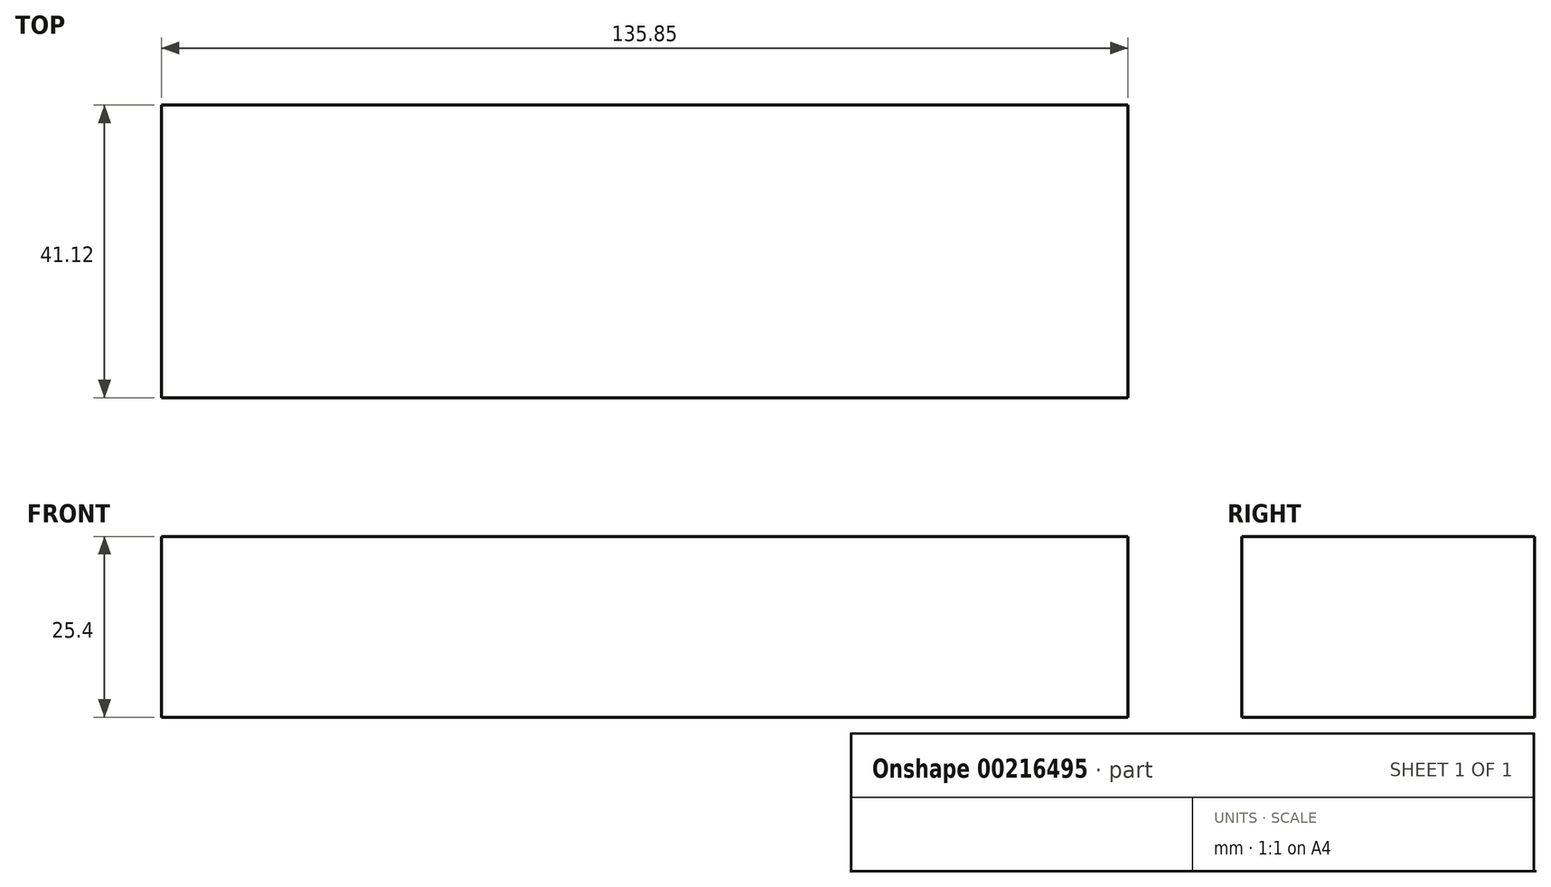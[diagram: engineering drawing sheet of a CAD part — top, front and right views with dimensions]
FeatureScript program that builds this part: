
annotation { "Feature Type Name" : "Feature", "Feature Type Description" : "" }
export const myFeature = defineFeature(function(context is Context, id is Id, definition is map)
    precondition{}
    {
        {
            var Q0;
            Q0=qCreatedBy(makeId("Top.planeOp"),FACE);
            var sketch = newSketch(context, id + "F0", { "sketchPlane" : qUnion([Q0])});
            skLineSegment(sketch, "E0.bottom", {"start": v(0, 0) * mm, "end": v(-135.85, 0) * mm});
            skLineSegment(sketch, "E0.top", {"start": v(0, 41.12) * mm, "end": v(-135.85, 41.12) * mm});
            skLineSegment(sketch, "E0.left", {"start": v(0, 0) * mm, "end": v(0, 41.12) * mm});
            skLineSegment(sketch, "E0.right", {"start": v(-135.85, 0) * mm, "end": v(-135.85, 41.12) * mm});
            skSolve(sketch);
        }
        {
            var Q0;
            Q0 = qSketchRegion(id + "F0", true);
            extrude(context, id + "F1", {"entities" : qUnion([Q0]), "oppositeDirection" : true, "depth" : 25.4 * mm});
        }
    });
